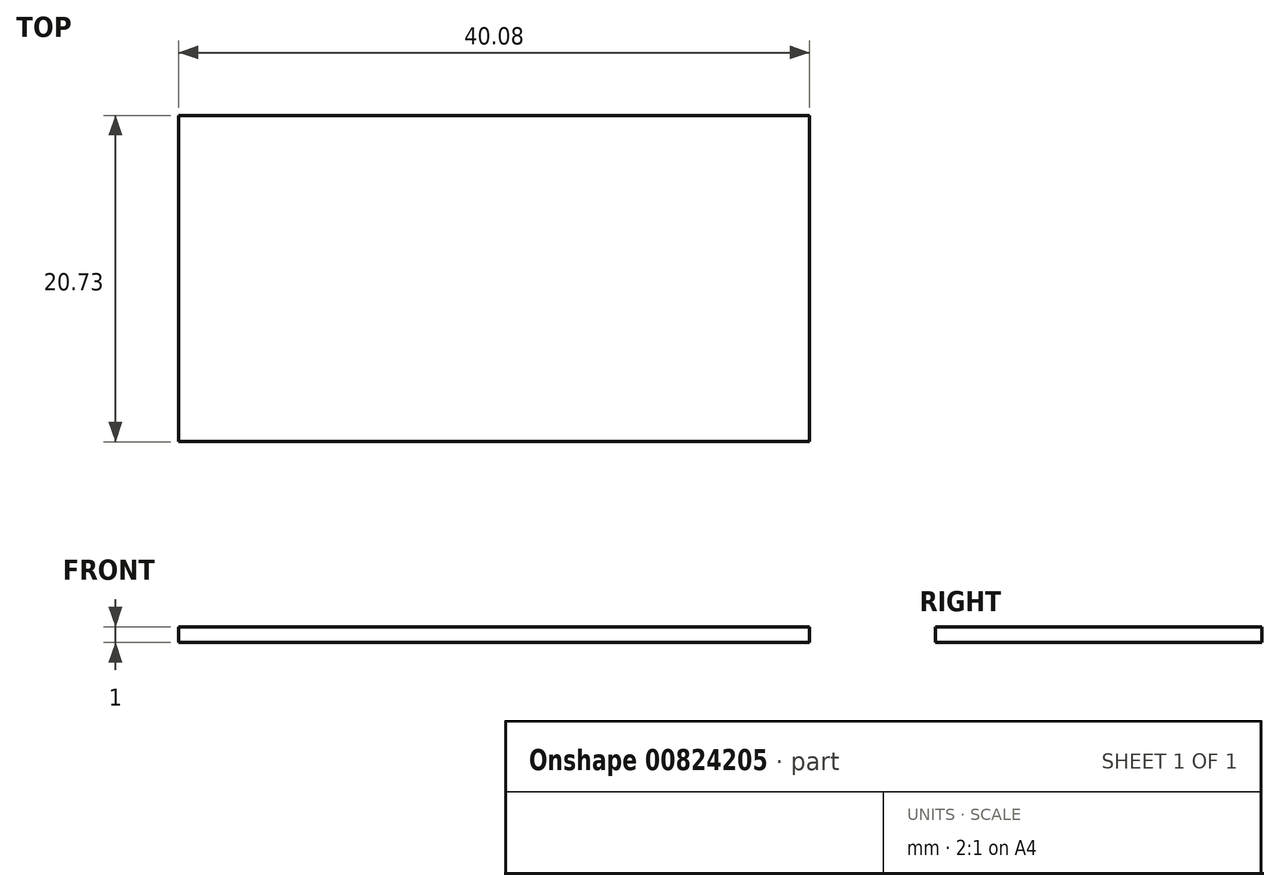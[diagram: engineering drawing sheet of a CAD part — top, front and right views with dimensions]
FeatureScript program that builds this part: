
annotation { "Feature Type Name" : "Feature", "Feature Type Description" : "" }
export const myFeature = defineFeature(function(context is Context, id is Id, definition is map)
    precondition{}
    {
        {
            var Q0;
            Q0=qCreatedBy(makeId("Top.planeOp"),FACE);
            var sketch = newSketch(context, id + "F0", { "sketchPlane" : qUnion([Q0])});
            skLineSegment(sketch, "E0.bottom", {"start": v(0, 0) * mm, "end": v(40.08, 0) * mm});
            skLineSegment(sketch, "E0.top", {"start": v(0, -20.73) * mm, "end": v(40.08, -20.73) * mm});
            skLineSegment(sketch, "E0.left", {"start": v(0, 0) * mm, "end": v(0, -20.73) * mm});
            skLineSegment(sketch, "E0.right", {"start": v(40.08, 0) * mm, "end": v(40.08, -20.73) * mm});
            skSolve(sketch);
        }
        {
            var Q0;
            Q0=makeQuery(id+"F0.imprint","IMPRINT",FACE,{"disambiguationData":[TD([[makeQuery(id+"F0.imprint","IMPRINT",EDGE,{"derivedFrom":sQuery(id+"F0.wireOp",EDGE,"E0.bottom")}),-1.0]])]});
            extrude(context, id + "F1", {"entities" : qUnion([Q0]), "depth" : 1 * mm, "offsetDistance" : 25 * mm});
        }
    });
